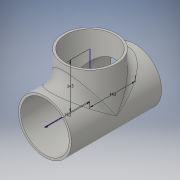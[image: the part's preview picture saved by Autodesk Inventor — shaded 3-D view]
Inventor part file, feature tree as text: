
AUTODESK INVENTOR PART (.ipt)
format: ipt  version: 2016 (Build 200138000, 138)  size: 176,128 bytes
history: native  units: in
note: dims shown in document units (in); Inventor stores cm internally (conversion verified against a paired STEP export)
features: sketch x6, extrude x4, fillet x1
ambient origin geometry x8: Origin, YZ Plane, XZ Plane, XY Plane, X Axis, Y Axis, Z Axis, Center Point
bodies: Body1 (feature_tree)
feature tree (11):
  sketch  "3D Sketch2"
  sketch  "Sketch6"  dims[d4=5.6299in d5=5.6299in]
  sketch  "Sketch7"  dims[d6=5.6299in d7=6.6142in]
  sketch  "Sketch8"  dims[d8=0.2799in d9=6.6142in]
  extrude  "Extrusion2"  Depth=5.6299in
  extrude  "Extrusion3"  Depth=6.6142in
  extrude  "Extrusion4"  Depth=6.6142in
  extrude  "Extrusion5"  Depth=11.2598in TaperAngle=0.0deg
  fillet  "Fillet1"  Radius=5.6299in
  sketch  "Sketch9"  dims[d10=0.2799in d11=11.2598in d12=0.0in d13=5.6299in d14=0.0in]
  sketch  "Sketch10"  dims[d15=11.811in d16=0.0in d17=5.6299in d18=0.0in d19=1.5748in]
